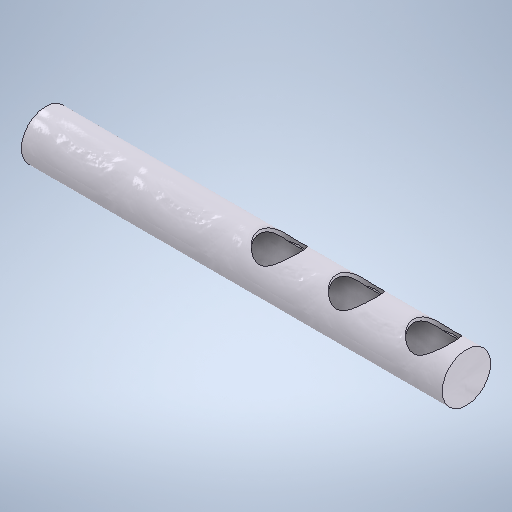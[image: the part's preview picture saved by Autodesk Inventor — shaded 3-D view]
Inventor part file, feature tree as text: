
AUTODESK INVENTOR PART (.ipt)
format: ipt  version: 2025.1 (Build 291241000, 241)  size: 309,760 bytes
history: native  units: mm
features: extrude x2, sketch x2, shell x1, plane x1, projected_geometry x1
ambient origin geometry x8: Origin, YZ Plane, XZ Plane, XY Plane, X Axis, Y Axis, Z Axis, Center Point
bodies: Volumenkörper1 (feature_tree)
feature tree (7):
  extrude  "Extrusion1"  Depth=191.0mm TaperAngle=0.0deg
  shell  "Wandung1"  Thickness=1.5mm
  plane  "Arbeitsebene1"
  extrude  "Extrusion2"  Depth=15.0mm
  sketch  "Skizze1"  dims[d0=22.0mm d2=191.0mm d3=0.0mm d4=1.5mm]
  sketch  "Skizze2"  dims[d5=11.0mm d6=15.0mm d7=35.0mm d8=35.0mm d9=18.0mm d10=6.0mm d11=0.0mm]
  projected_geometry  "Projizierte Kontur1"
